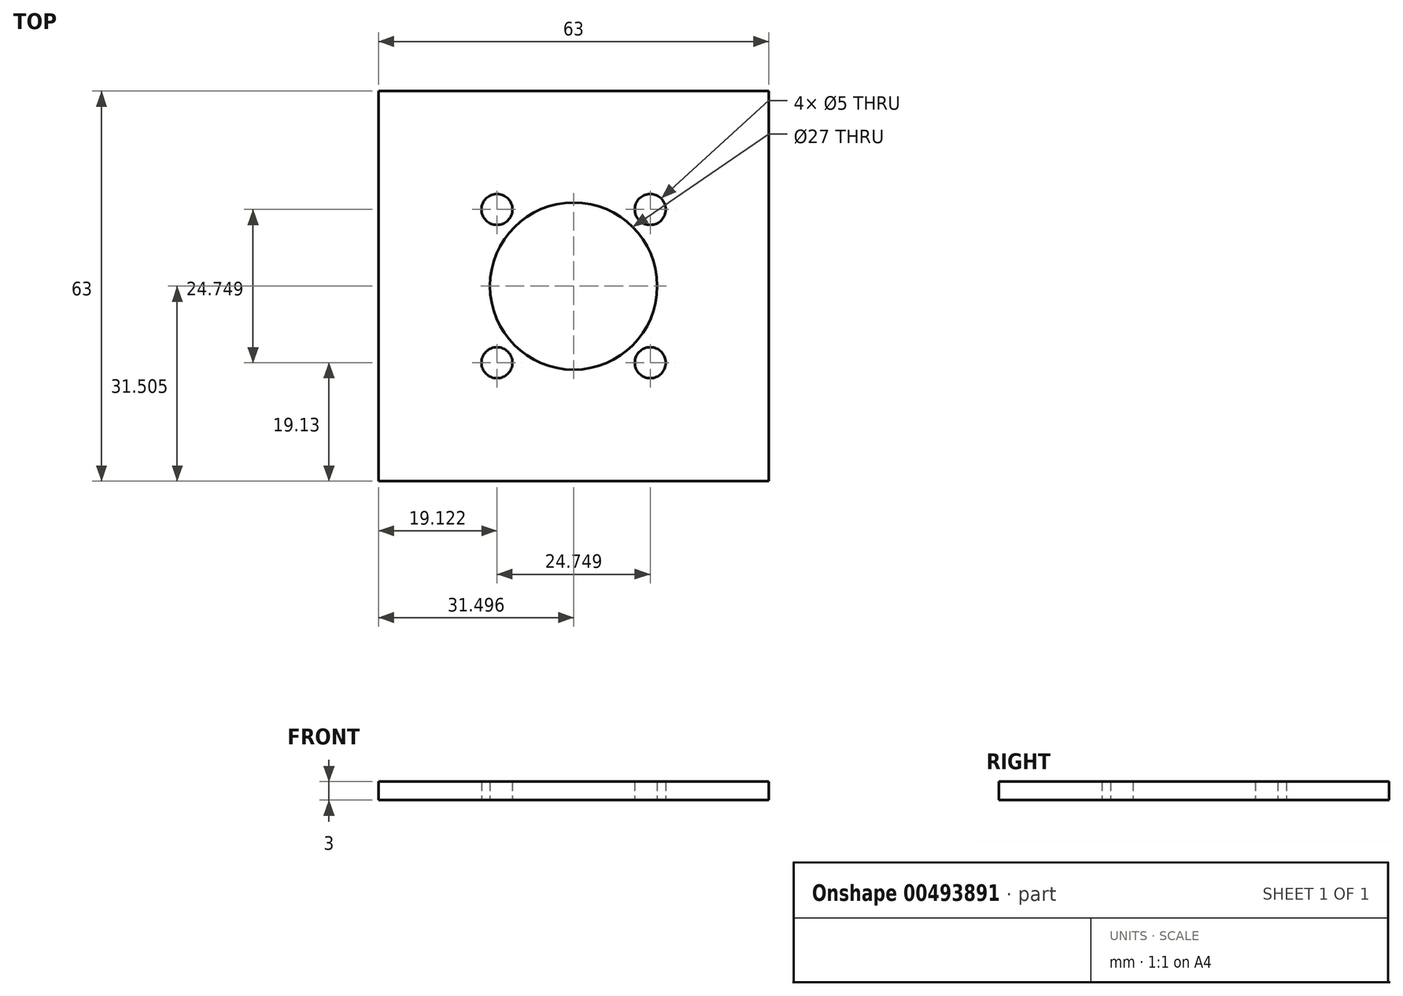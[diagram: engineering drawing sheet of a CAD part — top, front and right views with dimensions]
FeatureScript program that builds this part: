
annotation { "Feature Type Name" : "Feature", "Feature Type Description" : "" }
export const myFeature = defineFeature(function(context is Context, id is Id, definition is map)
    precondition{}
    {
        {
            var Q0;
            Q0=qCreatedBy(makeId("Top.planeOp"),FACE);
            var sketch = newSketch(context, id + "F0", { "sketchPlane" : qUnion([Q0])});
            skLineSegment(sketch, "E0.bottom", {"start": v(-25.81, 25.53) * mm, "end": v(37.19, 25.53) * mm});
            skLineSegment(sketch, "E0.top", {"start": v(-25.81, -37.47) * mm, "end": v(37.19, -37.47) * mm});
            skLineSegment(sketch, "E0.left", {"start": v(-25.81, 25.53) * mm, "end": v(-25.81, -37.47) * mm});
            skLineSegment(sketch, "E0.right", {"start": v(37.19, 25.53) * mm, "end": v(37.19, -37.47) * mm});
            skCircle(sketch, "E1", {"center": v(5.69, -5.97) * mm, "radius": 13.5 * mm});
            skCircle(sketch, "E2", {"center": v(-6.69, 6.4) * mm, "radius": 2.5 * mm});
            skCircle(sketch, "E3", {"center": v(18.06, 6.4) * mm, "radius": 2.5 * mm});
            skCircle(sketch, "E4", {"center": v(18.06, -18.34) * mm, "radius": 2.5 * mm});
            skCircle(sketch, "E5", {"center": v(-6.69, -18.34) * mm, "radius": 2.5 * mm});
            skSolve(sketch);
        }
        {
            var Q0;
            Q0=qSketchRegion(id+"F0",true);
            extrude(context, id + "F1", {"entities" : qUnion([Q0]), "depth" : 3 * mm});
        }
    });
